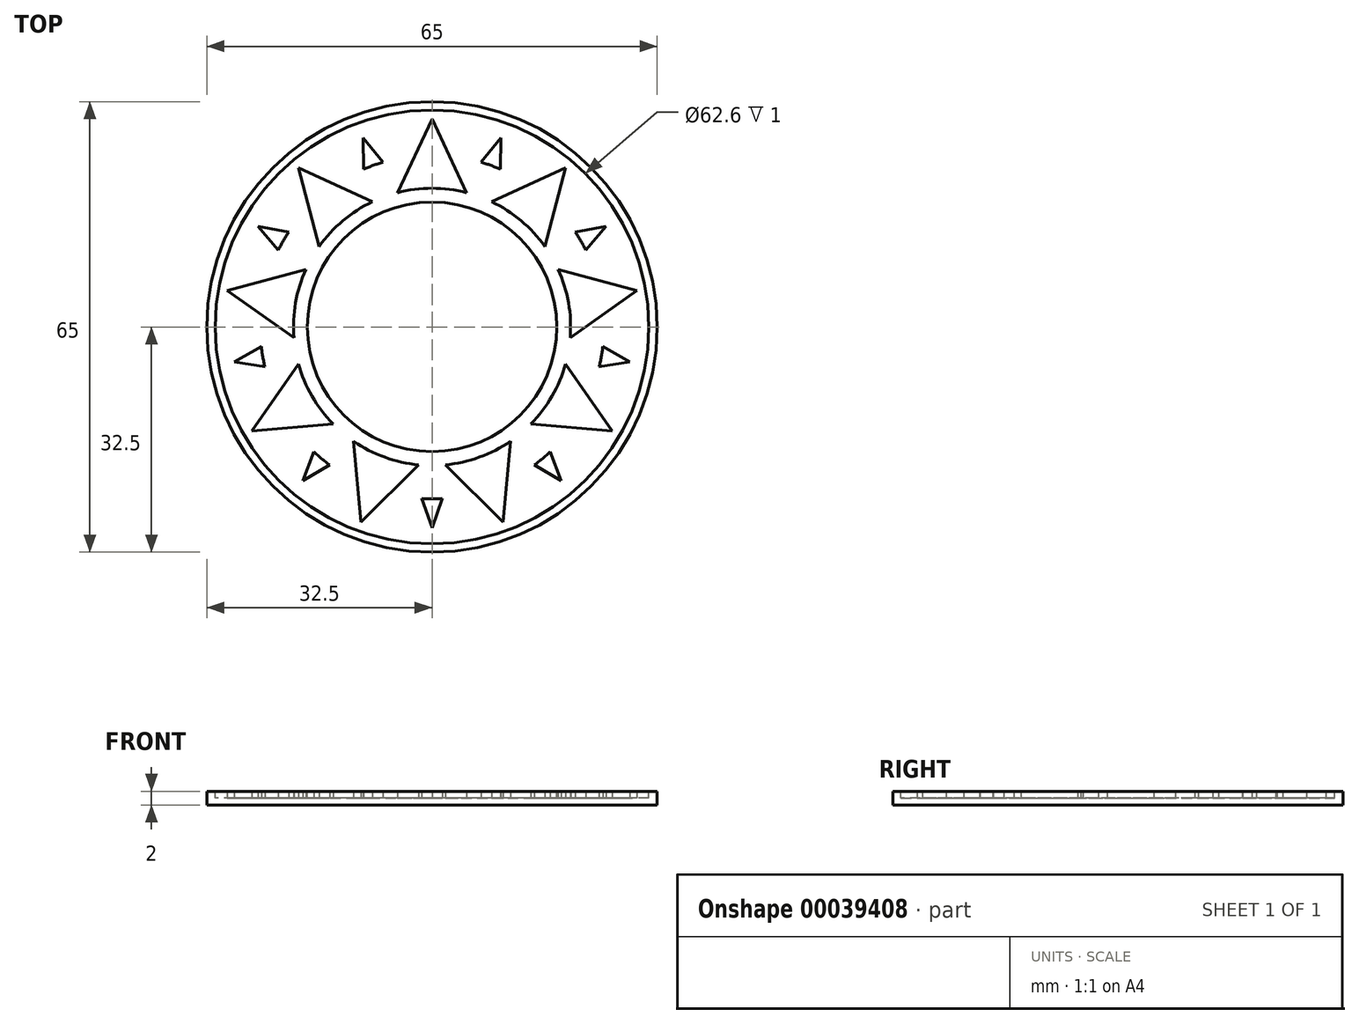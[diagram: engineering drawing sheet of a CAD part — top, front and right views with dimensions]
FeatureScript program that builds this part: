
annotation { "Feature Type Name" : "Feature", "Feature Type Description" : "" }
export const myFeature = defineFeature(function(context is Context, id is Id, definition is map)
    precondition{}
    {
        {
            var Q0;
            Q0=qCreatedBy(makeId("Top.planeOp"),FACE);
            var sketch = newSketch(context, id + "F0", { "sketchPlane" : qUnion([Q0])});
            skCircle(sketch, "E0", {"center": v(0, 0) * mm, "radius": 32.5 * mm});
            skSolve(sketch);
        }
        {
            var Q0;
            Q0=qSketchRegion(id+"F0",true);
            extrude(context, id + "F1", {"entities" : qUnion([Q0]), "depth" : 2 * mm});
        }
        {
            var Q0;
            Q0=makeQuery(id+"F1.opExtrude","CAP_FACE",FACE,{"disambiguationData":[OSD([sQuery(id+"F0.wireOp",EDGE,"E0")])],"isStart":false});
            var sketch = newSketch(context, id + "F2", { "sketchPlane" : qUnion([Q0])});
            skCircle(sketch, "E1", {"center": v(0, 0) * mm, "radius": 31.3 * mm});
            skCircle(sketch, "E2", {"center": v(0, 0) * mm, "radius": 18 * mm});
            skSolve(sketch);
        }
        {
            var Q0;
            Q0=qSketchRegion(id+"F2",true);
            extrude(context, id + "F3", {"entities" : qUnion([Q0]), "operationType" : NewBodyOperationType.REMOVE, "oppositeDirection" : true, "depth" : 1 * mm});
        }
        {
            var Q0;
            Q0=makeQuery(id+"F3.boolean.opBoolean","COPY",FACE,{"derivedFrom":makeQuery(id+"F3.opExtrude","CAP_FACE",FACE,{"disambiguationData":[OSD([sQuery(id+"F2.wireOp",EDGE,"E1"),sQuery(id+"F2.wireOp",EDGE,"E2")])],"isStart":false})});
            var sketch = newSketch(context, id + "F4", { "sketchPlane" : qUnion([Q0])});
            skArc(sketch, "E3", {"start": v(5, 19.36) * mm, "mid": v(0, 20) * mm, "end": v(-5, 19.36) * mm});
            skFitSpline(sketch, "E4", {"points": [v(-5, 19.36) * mm, v(0, 30) * mm], "startDerivative": vector(15, 31.9) * mm, "endDerivative": vector(15, 31.9) * mm});
            skFitSpline(sketch, "E5", {"points": [v(0, 30) * mm, v(5, 19.36) * mm], "startDerivative": vector(15, -31.9) * mm, "endDerivative": vector(15, -31.9) * mm});
            skLineSegment(sketch, "E6", {"start": v(0, 18) * mm, "end": v(0, 0) * mm, "construction": true});
            skLineSegment(sketch, "E7", {"start": v(0, 0) * mm, "end": v(10.7, 29.41) * mm, "construction": true});
            skLineSegment(sketch, "E8", {"start": v(9.92, 27.25) * mm, "end": v(7.06, 23.78) * mm});
            skLineSegment(sketch, "E9", {"start": v(9.88, 22.75) * mm, "end": v(9.92, 27.25) * mm});
            skArc(sketch, "E10", {"start": v(9.88, 22.75) * mm, "mid": v(8.48, 23.3) * mm, "end": v(7.06, 23.78) * mm});
            skSolve(sketch);
        }
        {
            var Q0;
            Q0=qSketchRegion(id+"F4",true);
            var Q1;
            Q1=makeQuery(id+"F3.boolean.opBoolean","SPLIT",FACE,{"disambiguationData":[TD([makeQuery(id+"F3.opExtrude","SWEPT_FACE",FACE,{"disambiguationData":[OSD([sQuery(id+"F2.wireOp",EDGE,"E2")])]})])],"derivedFrom":makeQuery(id+"F1.opExtrude","CAP_FACE",FACE,{"disambiguationData":[OSD([sQuery(id+"F0.wireOp",EDGE,"E0")])],"isStart":false})});
            extrude(context, id + "F5", {"entities" : qUnion([Q0]), "operationType" : NewBodyOperationType.ADD, "endBound" : BoundingType.UP_TO_SURFACE, "endBoundEntityFace" : qUnion([Q1]), "depth" : 25 * mm});
        }
        {
            var Q0;
            Q0=makeQuery(id+"F1.opExtrude","SWEPT_BODY",BODY,{"disambiguationData":[OSD([sQuery(id+"F0.wireOp",EDGE,"E0")])]});
            var Q1;
            Q1=makeQuery(id+"F1.opExtrude","SWEPT_FACE",FACE,{"disambiguationData":[OSD([sQuery(id+"F0.wireOp",EDGE,"E0")])]});
            circularPattern(context, id + "F6", {"operationType" : NewBodyOperationType.ADD, "entities" : qUnion([Q0]), "axis" : qUnion([Q1]), "angle" : 360 * degree, "instanceCount" : round(9), "equalSpace" : true});
        }
    });
